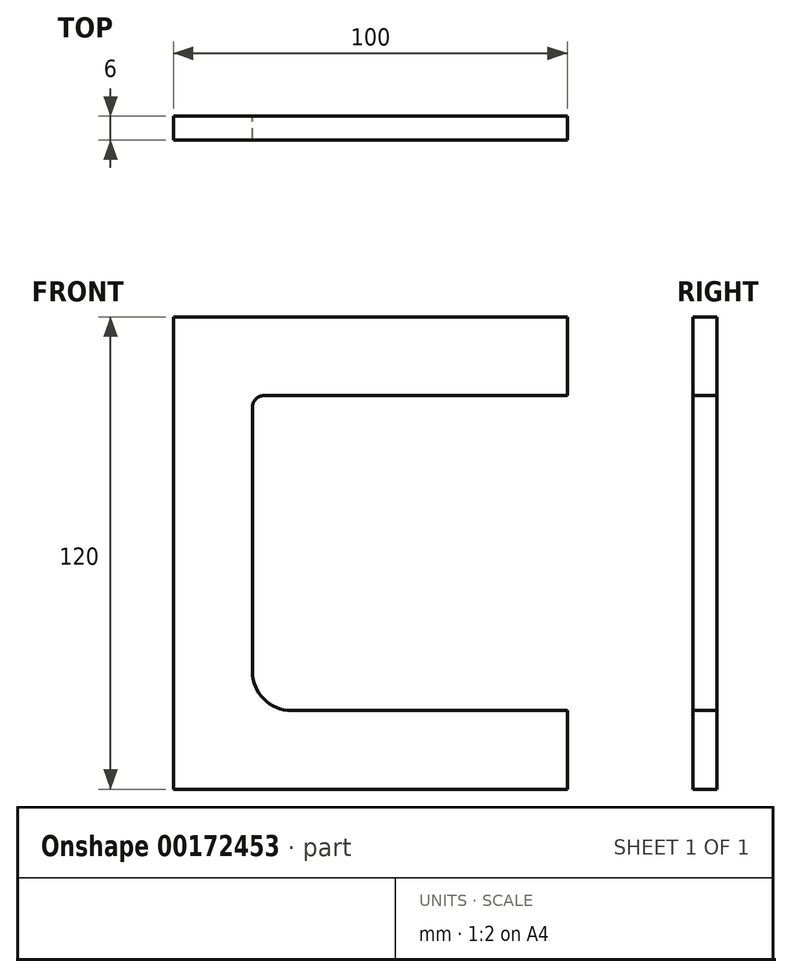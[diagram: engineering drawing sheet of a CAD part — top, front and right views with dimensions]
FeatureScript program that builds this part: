
annotation { "Feature Type Name" : "Feature", "Feature Type Description" : "" }
export const myFeature = defineFeature(function(context is Context, id is Id, definition is map)
    precondition{}
    {
        {
            var Q0;
            Q0=qCreatedBy(makeId("Front.planeOp"),FACE);
            var sketch = newSketch(context, id + "F0", { "sketchPlane" : qUnion([Q0])});
            skLineSegment(sketch, "E0", {"start": v(0, 60) * mm, "end": v(0, -60) * mm});
            skLineSegment(sketch, "E1", {"start": v(0, 60) * mm, "end": v(100, 60) * mm});
            skLineSegment(sketch, "E2", {"start": v(100, 60) * mm, "end": v(100, 40) * mm});
            skLineSegment(sketch, "E3", {"start": v(100, 40) * mm, "end": v(23, 40) * mm});
            skLineSegment(sketch, "E4", {"start": v(20, 37) * mm, "end": v(20, -30) * mm});
            skLineSegment(sketch, "E5", {"start": v(30, -40) * mm, "end": v(100, -40) * mm});
            skLineSegment(sketch, "E6", {"start": v(100, -40) * mm, "end": v(100, -60) * mm});
            skLineSegment(sketch, "E7", {"start": v(100, -60) * mm, "end": v(0, -60) * mm});
            skPoint(sketch, "E8.visualSharp", {"position": v(20, 40) * mm});
            skArc(sketch, "E8.filletArc", {"start": v(23, 40) * mm, "mid": v(20.88, 39.12) * mm, "end": v(20, 37) * mm});
            skPoint(sketch, "E9.visualSharp", {"position": v(20, -40) * mm});
            skArc(sketch, "E9.filletArc", {"start": v(20, -30) * mm, "mid": v(22.93, -37.07) * mm, "end": v(30, -40) * mm});
            skSolve(sketch);
        }
        {
            var Q0;
            Q0 = qSketchRegion(id + "F0", true);
            extrude(context, id + "F1", {"entities" : qUnion([Q0]), "depth" : 6 * mm});
        }
    });
